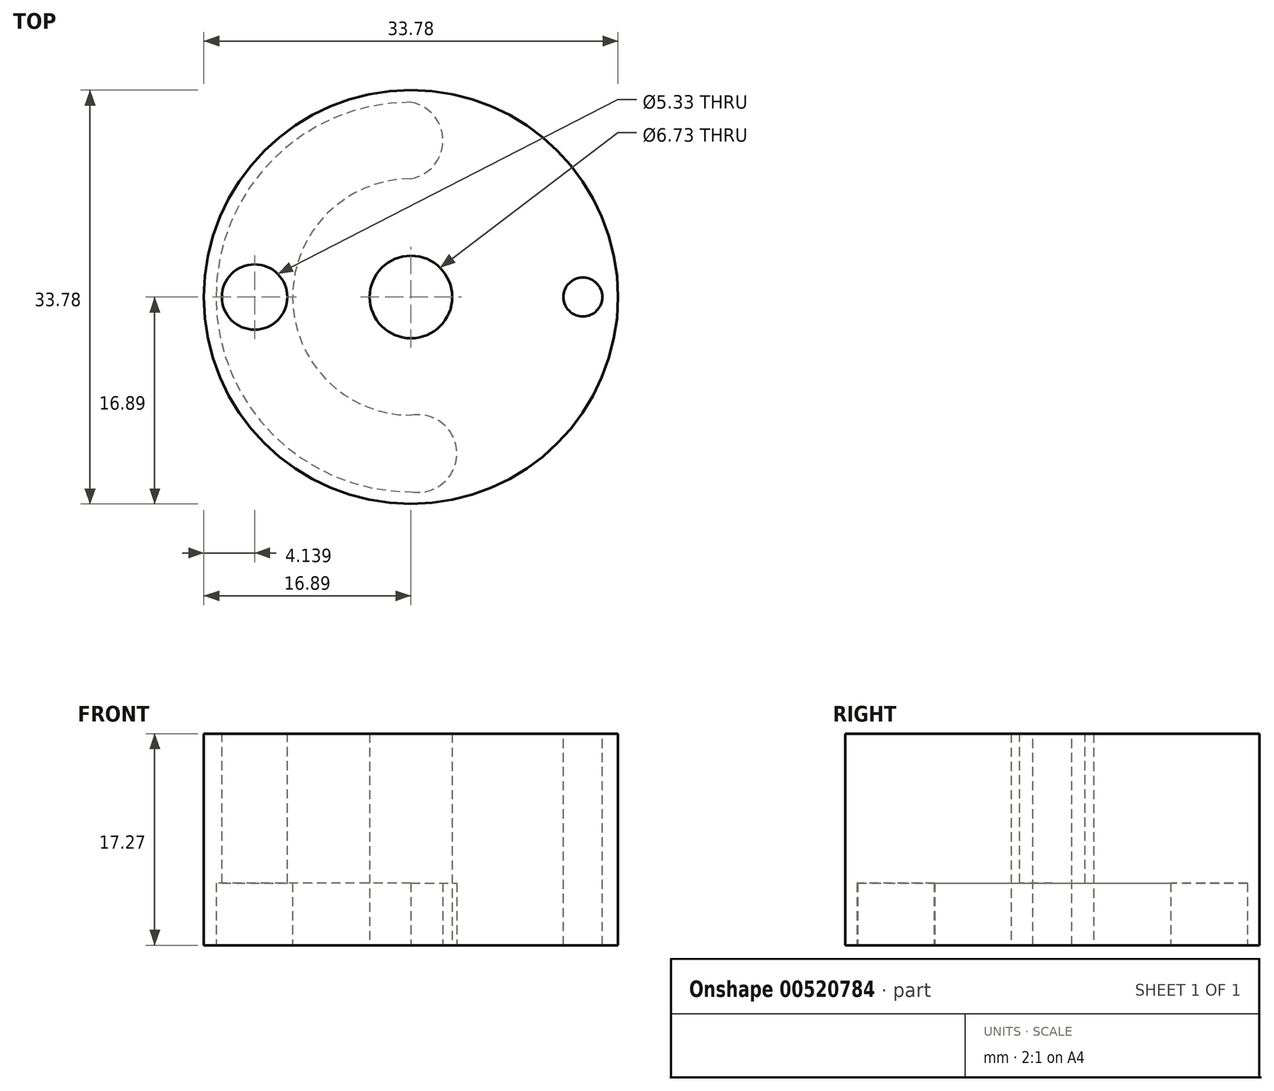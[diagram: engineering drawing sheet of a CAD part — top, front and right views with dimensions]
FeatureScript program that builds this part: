
annotation { "Feature Type Name" : "Feature", "Feature Type Description" : "" }
export const myFeature = defineFeature(function(context is Context, id is Id, definition is map)
    precondition{}
    {
        {
            var Q0;
            Q0=qCreatedBy(makeId("Top.planeOp"),FACE);
            var sketch = newSketch(context, id + "F0", { "sketchPlane" : qUnion([Q0])});
            skCircle(sketch, "E0", {"center": v(0, 0) * mm, "radius": 16.9 * mm});
            skCircle(sketch, "E1", {"center": v(0, 0) * mm, "radius": 3.37 * mm});
            skSolve(sketch);
        }
        {
            var Q0;
            Q0 = qSketchRegion(id + "F0", true);
            extrude(context, id + "F1", {"entities" : qUnion([Q0]), "depth" : 17.27 * mm, "offsetDistance" : 25.4 * mm});
        }
        {
            var Q0;
            Q0=makeQuery(id+"F1.opExtrude","CAP_FACE",FACE,{"disambiguationData":[OSD([sQuery(id+"F0.wireOp",EDGE,"E0"),sQuery(id+"F0.wireOp",EDGE,"E1")])],"isStart":false});
            var sketch = newSketch(context, id + "F2", { "sketchPlane" : qUnion([Q0])});
            skCircle(sketch, "E2", {"center": v(14.02, 0) * mm, "radius": 1.59 * mm});
            skCircle(sketch, "E3", {"center": v(-12.75, 0) * mm, "radius": 2.67 * mm});
            skSolve(sketch);
        }
        {
            var Q0;
            Q0 = qSketchRegion(id + "F2", true);
            extrude(context, id + "F3", {"entities" : qUnion([Q0]), "operationType" : NewBodyOperationType.REMOVE, "oppositeDirection" : true, "depth" : 25.4 * mm, "offsetDistance" : 25.4 * mm});
        }
        {
            var Q0;
            Q0=makeQuery(id+"F1.opExtrude","CAP_FACE",FACE,{"disambiguationData":[OSD([sQuery(id+"F0.wireOp",EDGE,"E0"),sQuery(id+"F0.wireOp",EDGE,"E1")])],"isStart":true});
            var sketch = newSketch(context, id + "F4", { "sketchPlane" : qUnion([Q0])});
            skArc(sketch, "E4", {"start": v(0, 9.65) * mm, "mid": v(-9.65, 0) * mm, "end": v(0, -9.65) * mm});
            skArc(sketch, "E5", {"start": v(0, 15.9) * mm, "mid": v(-15.9, 0) * mm, "end": v(0, -15.9) * mm});
            skArc(sketch, "E6", {"start": v(0, 9.65) * mm, "mid": v(3.74, 12.78) * mm, "end": v(0, 15.9) * mm});
            skArc(sketch, "E7", {"start": v(0, -15.9) * mm, "mid": v(2.6, -12.78) * mm, "end": v(0, -9.65) * mm});
            skSolve(sketch);
        }
        {
            var Q0;
            Q0 = qSketchRegion(id + "F4", true);
            extrude(context, id + "F5", {"entities" : qUnion([Q0]), "operationType" : NewBodyOperationType.REMOVE, "oppositeDirection" : true, "depth" : 5.08 * mm, "offsetDistance" : 25.4 * mm});
        }
    });
